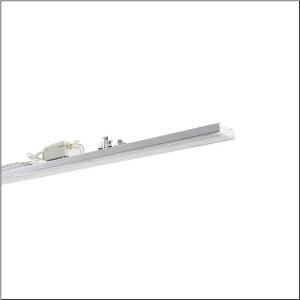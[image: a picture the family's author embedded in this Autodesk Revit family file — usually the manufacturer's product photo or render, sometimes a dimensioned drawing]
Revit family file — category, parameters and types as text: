
# Revit family: licross_r__21_recessed_mo_52te12cn49xg_2497
name_source: partatom
category: Lighting Fixtures
units: mm (PartAtom-declared; Revit-internal decimal feet)

## family parameters
Cut with Voids When Loaded = No
Host = Face
Light Source = No
Part Type = Normal
Room Calculation Point = No
Round Connector Dimension = Use Diameter
Shared = No

## types (1)
- --- (1 x LED, 9260 lm, 49.9 W, 4000K)
    Apparent Load = 50 VA
    CIE Flux Codes = 72 92 99 100 100
    Color Rendering = 80
    Color Temperature = 4000K
    Default Elevation = 1800 mm
    Description = Licross® 21 Recessed MO, luminaire insert, of sheet steel, galvanised, coil coated, white, length: 1.500mm, width: 66mm, height: 67mm, LED rated luminous flux: 9.260lm, light colour: 840, control gear: ON/OFF Multilumen, CLOi, control gear: ECG Multilumen, with plug, 3-pole, with phase selection, mains connection: 220..240V, AC, 50/60Hz, start of lifetime: 49W, end of service life: 61W, halogen-free wiring, primary optical cover: cover, of PMMA, light emission: direct distribution, primary light characteristic: symmetric, protection rating (complete): IP54, insulation class (complete): insulation class I (protective earthing), certification: CE, ENEC, VDE, UKCA, protection symbol: D if used in an environment with non-conductive dust loads with corresponding accessories, impact resistance: IK06, permissible ambient temperature for indoor applications: -35..+40°C, corresponds to IFS (International Featured Standards) requirements for safety and quality in the food industry, reducing of maximum allowable ambient temperature of 5°C with ceiling mounting, LABS conformity tested according to VDMA 24364:2018-05, packaging unit: 1 piece
    Height = 58 mm
    Lamp = 1 x LED
    Lamp Light Flux = 9260 lm
    Lamp Power = 49.9 W
    Lamp count = 1
    Length = 1500 mm
    Luminous efficacy = 186 lm/W
    Manufacturer = Siteco
    ModVariant = No
    Model = 52TE12CN49XG
    Mounting Place = Ceiling
    Mounting Type = Pendant
    Number of Poles = 1
    OnlyDefault = Yes
    Power Factor = 1
    Product Name = Licross® 21 Recessed MO
    Product group = luminaire insert
    ProductGroupID = 901
    Protection Class = Protection class I
    Protection Degree = IP 54
    RLX_Detail_Level = 1
    RLX_Emergency_Light_Flux = 0 lm
    RLX_Emergency_Type = 0
    RLX_Emergency_Type_DB = No
    RlxData = <blob elided: 22309 chars, md5=3c464dff>
    Socket = socket
    Standby Power = 0 W
    System Light Flux = 9260 lm
    System Power = 50 W
    Type Comments = factory setting: luminous flux: 100 % | (A | C | E) | 116 mA
    Type Image = l_1296930.jpg
    URL = http://relux.com
    VarID = @adj_040705
    Voltage = 0 V
    Weight = 0.00 kg
    Width = 66 mm

## geometry (parser evidence)
native form markers: Blend x4, Sweep x10
no freeform markers — native parametric forms only
